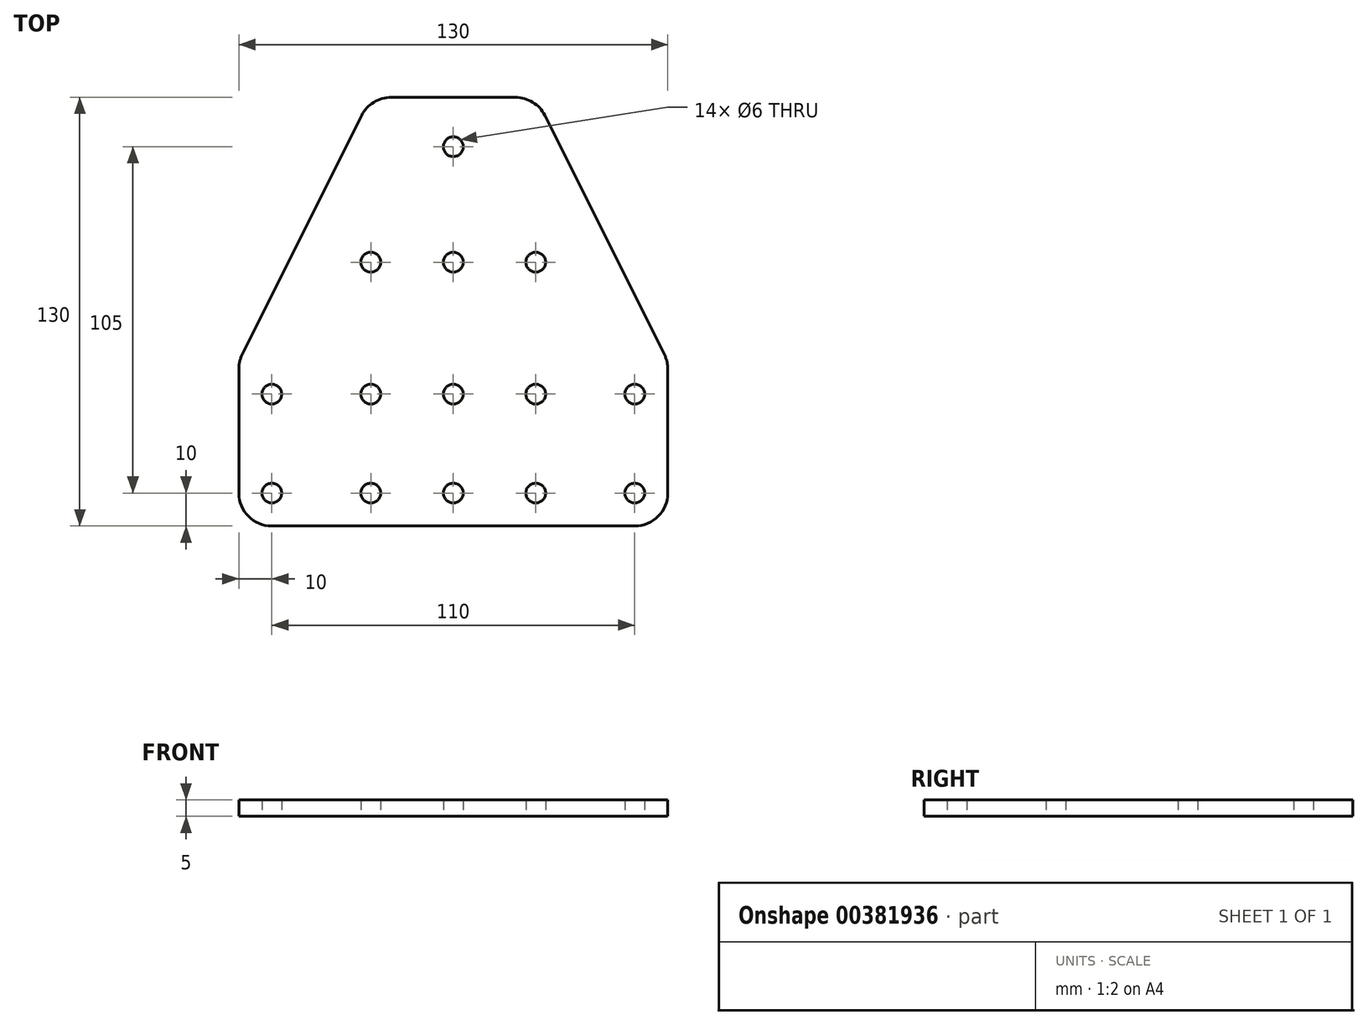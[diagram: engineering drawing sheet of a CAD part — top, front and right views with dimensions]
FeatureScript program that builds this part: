
annotation { "Feature Type Name" : "Feature", "Feature Type Description" : "" }
export const myFeature = defineFeature(function(context is Context, id is Id, definition is map)
    precondition{}
    {
        {
            assignVariable(context, id + "F0", {"name" : "Espessura", "anyValue" : 5});
        }
        {
            var Q0;
            Q0=qCreatedBy(makeId("Top.planeOp"),FACE);
            var sketch = newSketch(context, id + "F1", { "sketchPlane" : qUnion([Q0])});
            skLineSegment(sketch, "E0.bottom", {"start": v(65, 65) * mm, "end": v(-65, 65) * mm, "construction": true});
            skLineSegment(sketch, "E0.top", {"start": v(65, -65) * mm, "end": v(-65, -65) * mm, "construction": true});
            skLineSegment(sketch, "E0.left", {"start": v(65, 65) * mm, "end": v(65, -65) * mm, "construction": true});
            skLineSegment(sketch, "E0.right", {"start": v(-65, 65) * mm, "end": v(-65, -65) * mm, "construction": true});
            skPoint(sketch, "E0.middle", {"position": v(0, 0) * mm});
            skLineSegment(sketch, "E1", {"start": v(-65, -55) * mm, "end": v(65, -55) * mm, "construction": true});
            skLineSegment(sketch, "E2", {"start": v(-65, -25) * mm, "end": v(65, -25) * mm, "construction": true});
            skLineSegment(sketch, "E3", {"start": v(-65, 55) * mm, "end": v(65, 55) * mm, "construction": true});
            skLineSegment(sketch, "E4", {"start": v(-55, 65) * mm, "end": v(-55, -65) * mm, "construction": true});
            skLineSegment(sketch, "E5", {"start": v(55, 65) * mm, "end": v(55, -65) * mm, "construction": true});
            skLineSegment(sketch, "E6", {"start": v(0, -65) * mm, "end": v(0, 65) * mm, "construction": true});
            skLineSegment(sketch, "E7", {"start": v(-25, 65) * mm, "end": v(-25, -65) * mm, "construction": true});
            skLineSegment(sketch, "E8", {"start": v(25, 65) * mm, "end": v(25, -65) * mm, "construction": true});
            skLineSegment(sketch, "E9", {"start": v(-65, -15) * mm, "end": v(65, -15) * mm, "construction": true});
            skLineSegment(sketch, "E10", {"start": v(-65, -15) * mm, "end": v(-25, 65) * mm});
            skLineSegment(sketch, "E11", {"start": v(-25, 65) * mm, "end": v(25, 65) * mm});
            skLineSegment(sketch, "E12", {"start": v(25, 65) * mm, "end": v(65, -15) * mm});
            skLineSegment(sketch, "E13", {"start": v(65, -15) * mm, "end": v(65, -65) * mm});
            skLineSegment(sketch, "E14", {"start": v(65, -65) * mm, "end": v(-65, -65) * mm});
            skLineSegment(sketch, "E15", {"start": v(-65, -65) * mm, "end": v(-65, -15) * mm});
            skPoint(sketch, "E16", {"position": v(0, 50) * mm});
            skPoint(sketch, "E17", {"position": v(-55, -25) * mm});
            skPoint(sketch, "E18", {"position": v(-25, -25) * mm});
            skPoint(sketch, "E19", {"position": v(-25, -55) * mm});
            skPoint(sketch, "E20", {"position": v(-55, -55) * mm});
            skPoint(sketch, "E21", {"position": v(25, -55) * mm});
            skPoint(sketch, "E22", {"position": v(55, -55) * mm});
            skPoint(sketch, "E23", {"position": v(55, -25) * mm});
            skPoint(sketch, "E24", {"position": v(25, -25) * mm});
            skPoint(sketch, "E25", {"position": v(0, -55) * mm});
            skPoint(sketch, "E26", {"position": v(0, -25) * mm});
            skLineSegment(sketch, "E27", {"start": v(-25, 15) * mm, "end": v(25, 15) * mm, "construction": true});
            skPoint(sketch, "E28", {"position": v(25, 15) * mm});
            skPoint(sketch, "E29", {"position": v(0, 15) * mm});
            skPoint(sketch, "E30", {"position": v(-25, 15) * mm});
            skSolve(sketch);
        }
        {
            var Q0;
            Q0=makeQuery(id+"F1.imprint","IMPRINT",FACE,{"disambiguationData":[TD([[makeQuery(id+"F1.imprint","IMPRINT",EDGE,{"derivedFrom":sQuery(id+"F1.wireOp",EDGE,"E10")}),-1.0]])]});
            extrude(context, id + "F2", {"entities" : qUnion([Q0]), "depth" : (getVariable(context, 'Espessura')) * mm});
        }
        {
            var Q0;
            Q0=makeQuery(id+"F2.opExtrude","SWEPT_EDGE",EDGE,{"disambiguationData":[OSD([sQuery(id+"F1.wireOp",EDGE,"E14"),sQuery(id+"F1.wireOp",EDGE,"E15")])]});
            var Q1;
            Q1=makeQuery(id+"F2.opExtrude","SWEPT_EDGE",EDGE,{"disambiguationData":[OSD([sQuery(id+"F1.wireOp",EDGE,"E10"),sQuery(id+"F1.wireOp",EDGE,"E15")])]});
            var Q2;
            Q2=makeQuery(id+"F2.opExtrude","SWEPT_EDGE",EDGE,{"disambiguationData":[OSD([sQuery(id+"F1.wireOp",EDGE,"E10"),sQuery(id+"F1.wireOp",EDGE,"E11")])]});
            var Q3;
            Q3=makeQuery(id+"F2.opExtrude","SWEPT_EDGE",EDGE,{"disambiguationData":[OSD([sQuery(id+"F1.wireOp",EDGE,"E11"),sQuery(id+"F1.wireOp",EDGE,"E12")])]});
            var Q4;
            Q4=makeQuery(id+"F2.opExtrude","SWEPT_EDGE",EDGE,{"disambiguationData":[OSD([sQuery(id+"F1.wireOp",EDGE,"E12"),sQuery(id+"F1.wireOp",EDGE,"E13")])]});
            var Q5;
            Q5=makeQuery(id+"F2.opExtrude","SWEPT_EDGE",EDGE,{"disambiguationData":[OSD([sQuery(id+"F1.wireOp",EDGE,"E13"),sQuery(id+"F1.wireOp",EDGE,"E14")])]});
            fillet(context, id + "F3", {"entities" : qUnion([Q0, Q1, Q2, Q3, Q4, Q5]), "radius" : 10 * mm, "tangentPropagation" : true, "allowEdgeOverflow" : false});
        }
        {
            var Q0;
            Q0=sQuery(id+"F1.wireOp",VERTEX,"E17");
            var Q1;
            Q1=sQuery(id+"F1.wireOp",VERTEX,"E18");
            var Q2;
            Q2=sQuery(id+"F1.wireOp",VERTEX,"E20");
            var Q3;
            Q3=sQuery(id+"F1.wireOp",VERTEX,"E19");
            var Q4;
            Q4=sQuery(id+"F1.wireOp",VERTEX,"E21");
            var Q5;
            Q5=sQuery(id+"F1.wireOp",VERTEX,"E24");
            var Q6;
            Q6=sQuery(id+"F1.wireOp",VERTEX,"E23");
            var Q7;
            Q7=sQuery(id+"F1.wireOp",VERTEX,"E22");
            var Q8;
            Q8=sQuery(id+"F1.wireOp",VERTEX,"E16");
            var Q9;
            Q9=sQuery(id+"F1.wireOp",VERTEX,"E25");
            var Q10;
            Q10=sQuery(id+"F1.wireOp",VERTEX,"E26");
            var Q11;
            Q11=sQuery(id+"F1.wireOp",VERTEX,"E28");
            var Q12;
            Q12=sQuery(id+"F1.wireOp",VERTEX,"E29");
            var Q13;
            Q13=sQuery(id+"F1.wireOp",VERTEX,"E30");
            var Q14;
            Q14=makeQuery(id+"F2.opExtrude","SWEPT_BODY",BODY,{"disambiguationData":[OSD([sQuery(id+"F1.wireOp",EDGE,"E10"),sQuery(id+"F1.wireOp",EDGE,"E11"),sQuery(id+"F1.wireOp",EDGE,"E12"),sQuery(id+"F1.wireOp",EDGE,"E13"),sQuery(id+"F1.wireOp",EDGE,"E14"),sQuery(id+"F1.wireOp",EDGE,"E15")])]});
            hole(context, id + "F4", {"style" : HoleStyle.SIMPLE, "endStyle" : HoleEndStyle.THROUGH, "oppositeDirection" : true, "holeDiameter" : 6 * mm, "isTappedThrough" : true, "tappedDepth" : 12 * mm, "tapClearance" : 3, "locations" : qUnion([Q0, Q1, Q2, Q3, Q4, Q5, Q6, Q7, Q8, Q9, Q10, Q11, Q12, Q13]), "scope" : qUnion([Q14])});
        }
    });
